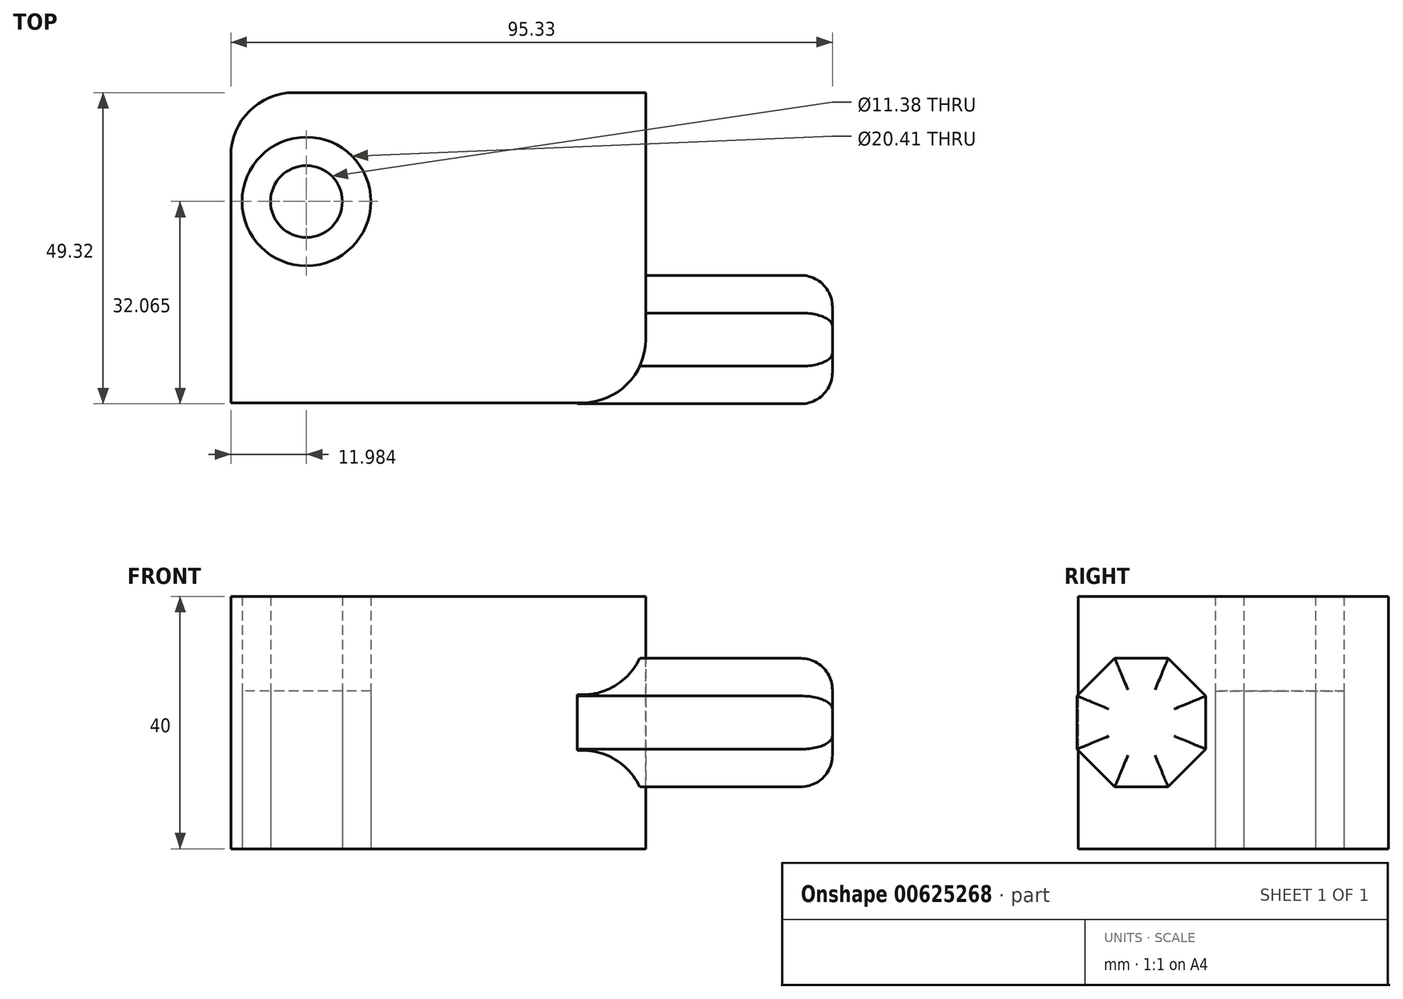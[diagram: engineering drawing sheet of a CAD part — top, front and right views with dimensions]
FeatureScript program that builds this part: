
annotation { "Feature Type Name" : "Feature", "Feature Type Description" : "" }
export const myFeature = defineFeature(function(context is Context, id is Id, definition is map)
    precondition{}
    {
        {
            var Q0;
            Q0=qCreatedBy(makeId("Top.planeOp"),FACE);
            var sketch = newSketch(context, id + "F0", { "sketchPlane" : qUnion([Q0])});
            skLineSegment(sketch, "E0.bottom", {"start": v(-24.83, 35.43) * mm, "end": v(30.9, 35.43) * mm});
            skLineSegment(sketch, "E0.top", {"start": v(-34.83, -13.7) * mm, "end": v(20.9, -13.7) * mm});
            skLineSegment(sketch, "E0.left", {"start": v(-34.83, 25.43) * mm, "end": v(-34.83, -13.7) * mm});
            skLineSegment(sketch, "E0.right", {"start": v(30.9, 35.43) * mm, "end": v(30.9, -3.7) * mm});
            skCircle(sketch, "E1", {"center": v(-22.85, 18.17) * mm, "radius": 10.2 * mm});
            skCircle(sketch, "E2", {"center": v(-22.85, 18.17) * mm, "radius": 5.69 * mm});
            skPoint(sketch, "E3.visualSharp", {"position": v(-34.83, 35.43) * mm});
            skArc(sketch, "E3.filletArc", {"start": v(-24.83, 35.43) * mm, "mid": v(-31.9, 32.5) * mm, "end": v(-34.83, 25.43) * mm});
            skPoint(sketch, "E4.visualSharp", {"position": v(30.9, -13.7) * mm});
            skArc(sketch, "E4.filletArc", {"start": v(20.9, -13.7) * mm, "mid": v(27.97, -10.78) * mm, "end": v(30.9, -3.7) * mm});
            skSolve(sketch);
        }
        {
            var Q0;
            Q0 = qSketchRegion(id + "F0", true);
            var Q1;
            Q1=makeQuery(id+"F0.imprint","IMPRINT",FACE,{"disambiguationData":[TD([[makeQuery(id+"F0.imprint","IMPRINT",EDGE,{"derivedFrom":sQuery(id+"F0.wireOp",EDGE,"E2")}),1.0]])]});
            extrude(context, id + "F1", {"entities" : qUnion([Q0, Q1]), "depth" : 40 * mm, "offsetDistance" : 25.4 * mm});
        }
        {
            var Q0;
            Q0=makeQuery(id+"F0.imprint","IMPRINT",FACE,{"disambiguationData":[TD([[makeQuery(id+"F0.imprint","IMPRINT",EDGE,{"derivedFrom":sQuery(id+"F0.wireOp",EDGE,"E1")}),1.0]])]});
            extrude(context, id + "F2", {"entities" : qUnion([Q0]), "depth" : 25 * mm, "offsetDistance" : 25 * mm});
        }
        {
            var Q0;
            Q0=makeQuery(id+"F1.opExtrude","SWEPT_FACE",FACE,{"disambiguationData":[OSD([sQuery(id+"F0.wireOp",EDGE,"E0.right")])]});
            var sketch = newSketch(context, id + "F3", { "sketchPlane" : qUnion([Q0])});
            skCircle(sketch, "E5.cCircle", {"center": v(-3.7, 20) * mm, "radius": 10.18 * mm, "construction": true});
            skLineSegment(sketch, "E5.0", {"start": v(-13.9, 15.78) * mm, "end": v(-13.9, 24.22) * mm});
            skLineSegment(sketch, "E5.1", {"start": v(-13.9, 24.22) * mm, "end": v(-7.93, 30.18) * mm});
            skLineSegment(sketch, "E5.2", {"start": v(-7.93, 30.18) * mm, "end": v(0.51, 30.18) * mm});
            skLineSegment(sketch, "E5.3", {"start": v(0.51, 30.18) * mm, "end": v(6.48, 24.22) * mm});
            skLineSegment(sketch, "E5.4", {"start": v(6.48, 24.22) * mm, "end": v(6.48, 15.78) * mm});
            skLineSegment(sketch, "E5.5", {"start": v(6.48, 15.78) * mm, "end": v(0.51, 9.82) * mm});
            skLineSegment(sketch, "E5.6", {"start": v(0.51, 9.82) * mm, "end": v(-7.93, 9.82) * mm});
            skLineSegment(sketch, "E5.7", {"start": v(-7.93, 9.82) * mm, "end": v(-13.9, 15.78) * mm});
            skPoint(sketch, "E5.0.midPoint", {"position": v(-13.9, 20) * mm});
            skSolve(sketch);
        }
        {
            var Q0;
            Q0=makeQuery(id+"F3.imprint","IMPRINT",FACE,{"disambiguationData":[TD([[makeQuery(id+"F3.imprint","IMPRINT",EDGE,{"derivedFrom":sQuery(id+"F3.wireOp",EDGE,"E5.0")}),-1.0]])]});
            var Q1;
            {var subQ1=sQuery(id+"F3.wireOp",EDGE,"E5.3");Q1=makeQuery(id+"F3.imprint","IMPRINT",FACE,{"disambiguationData":[TD([[makeQuery(id+"F3.imprint","IMPRINT",EDGE,{"derivedFrom":subQ1}),-1.0]])]});}
            extrude(context, id + "F4", {"entities" : qUnion([Q0, Q1]), "operationType" : NewBodyOperationType.ADD, "depth" : 29.6 * mm, "offsetDistance" : 25 * mm, "hasSecondDirection" : true, "secondDirectionOppositeDirection" : true, "secondDirectionDepth" : 10.8 * mm});
        }
        {
            var Q0;
            Q0=makeQuery(id+"F4.opExtrude","CAP_EDGE",EDGE,{"disambiguationData":[OSD([sQuery(id+"F3.wireOp",EDGE,"E5.7")])],"isStart":false});
            var Q1;
            Q1=makeQuery(id+"F4.opExtrude","CAP_EDGE",EDGE,{"disambiguationData":[OSD([sQuery(id+"F3.wireOp",EDGE,"E5.6")])],"isStart":false});
            var Q2;
            Q2=makeQuery(id+"F4.opExtrude","CAP_EDGE",EDGE,{"disambiguationData":[OSD([sQuery(id+"F3.wireOp",EDGE,"E5.0")])],"isStart":false});
            var Q3;
            Q3=makeQuery(id+"F4.opExtrude","CAP_EDGE",EDGE,{"disambiguationData":[OSD([sQuery(id+"F3.wireOp",EDGE,"E5.1")])],"isStart":false});
            var Q4;
            Q4=makeQuery(id+"F4.opExtrude","CAP_EDGE",EDGE,{"disambiguationData":[OSD([sQuery(id+"F3.wireOp",EDGE,"E5.2")])],"isStart":false});
            var Q5;
            Q5=makeQuery(id+"F4.opExtrude","CAP_EDGE",EDGE,{"disambiguationData":[OSD([sQuery(id+"F3.wireOp",EDGE,"E5.5")])],"isStart":false});
            var Q6;
            Q6=makeQuery(id+"F4.opExtrude","CAP_EDGE",EDGE,{"disambiguationData":[OSD([sQuery(id+"F3.wireOp",EDGE,"E5.4")])],"isStart":false});
            var Q7;
            Q7=makeQuery(id+"F4.opExtrude","CAP_EDGE",EDGE,{"disambiguationData":[OSD([sQuery(id+"F3.wireOp",EDGE,"E5.3")])],"isStart":false});
            fillet(context, id + "F5", {"entities" : qUnion([Q0, Q1, Q2, Q3, Q4, Q5, Q6, Q7]), "radius" : 5 * mm, "tangentPropagation" : true, "allowEdgeOverflow" : false});
        }
    });
